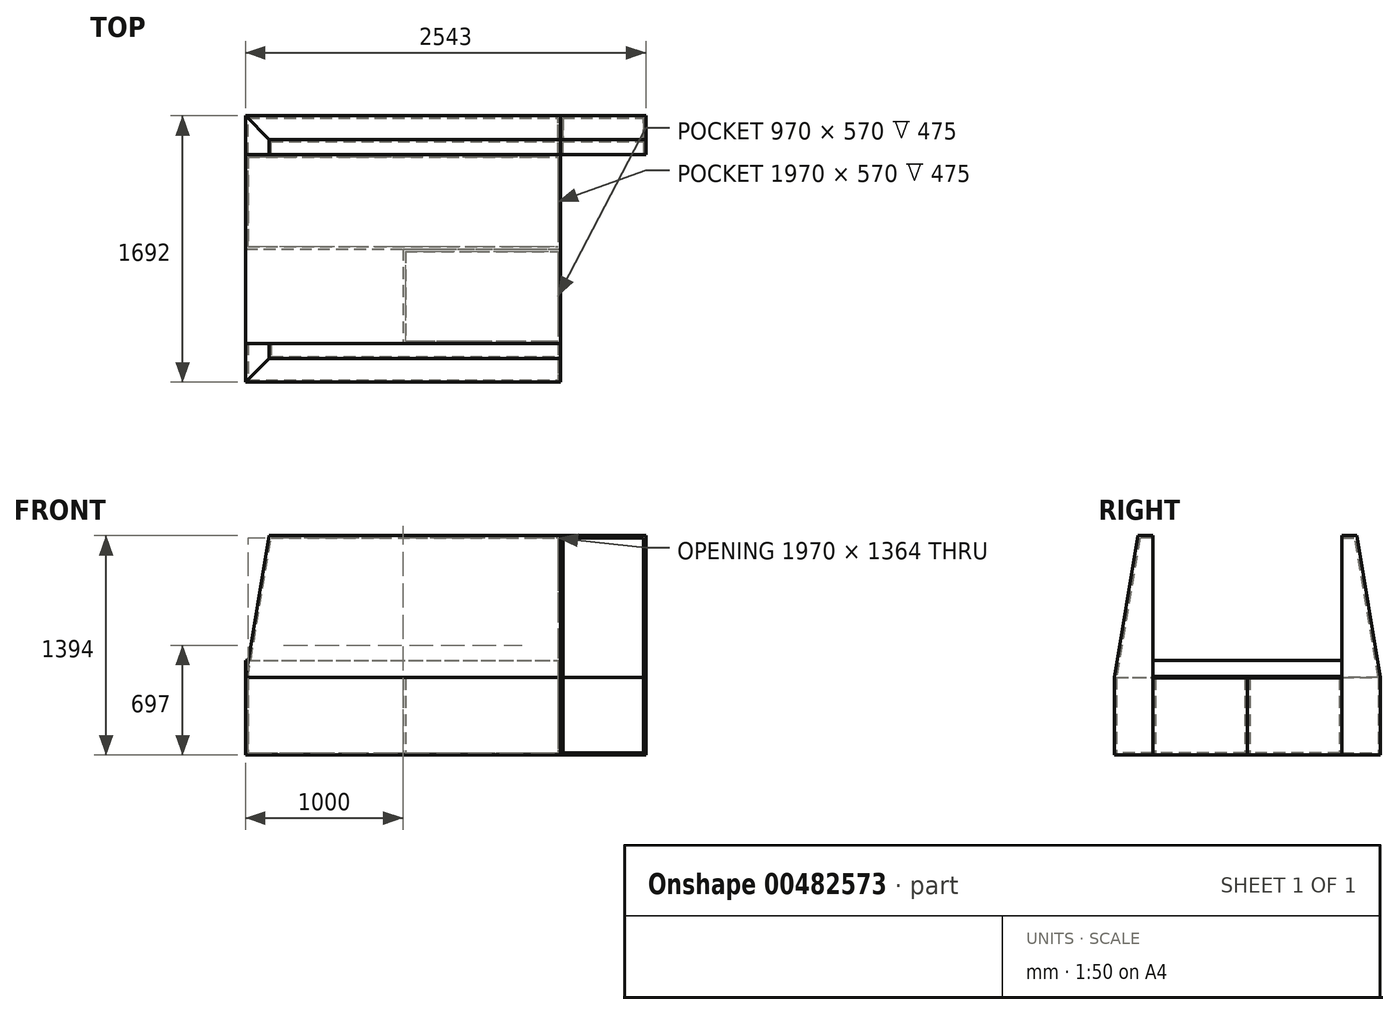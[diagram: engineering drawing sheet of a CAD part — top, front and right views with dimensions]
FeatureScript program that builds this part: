
annotation { "Feature Type Name" : "Feature", "Feature Type Description" : "" }
export const myFeature = defineFeature(function(context is Context, id is Id, definition is map)
    precondition{}
    {
        {
            var Q0;
            Q0=qCreatedBy(makeId("Top.planeOp"),FACE);
            var sketch = newSketch(context, id + "F0", { "sketchPlane" : qUnion([Q0])});
            skLineSegment(sketch, "E0.bottom", {"start": v(1471.5, -846) * mm, "end": v(-1471.5, -846) * mm, "construction": true});
            skLineSegment(sketch, "E0.top", {"start": v(1471.5, 846) * mm, "end": v(-1471.5, 846) * mm, "construction": true});
            skLineSegment(sketch, "E0.left", {"start": v(1471.5, -846) * mm, "end": v(1471.5, 846) * mm, "construction": true});
            skLineSegment(sketch, "E0.right", {"start": v(-1471.5, -846) * mm, "end": v(-1471.5, 846) * mm, "construction": true});
            skLineSegment(sketch, "E1", {"start": v(1071.5, 846) * mm, "end": v(1071.5, -846) * mm, "construction": true});
            skSolve(sketch);
        }
        {
            var Q0;
            Q0=qCreatedBy(makeId("Top.planeOp"),FACE);
            cPlane(context, id + "F1", {"entities" : qUnion([Q0]), "cplaneType" : CPlaneType.OFFSET, "offset" : 1394 * mm, "width" : 150 * mm, "height" : 150 * mm});
        }
        {
            var Q0;
            Q0=qCreatedBy(makeId("Top.planeOp"),FACE);
            var sketch = newSketch(context, id + "F2", { "sketchPlane" : qUnion([Q0])});
            skLineSegment(sketch, "E2.bottom", {"start": v(-1471.5, 600) * mm, "end": v(528.5, 600) * mm});
            skLineSegment(sketch, "E2.top", {"start": v(-1471.5, -600) * mm, "end": v(528.5, -600) * mm});
            skLineSegment(sketch, "E2.left", {"start": v(-1471.5, 600) * mm, "end": v(-1471.5, -600) * mm});
            skLineSegment(sketch, "E2.right", {"start": v(528.5, 600) * mm, "end": v(528.5, -600) * mm});
            skPoint(sketch, "E3", {"position": v(-1471.5, 0) * mm});
            skLineSegment(sketch, "E4.top", {"start": v(-1471.5, 846) * mm, "end": v(528.5, 846) * mm});
            skLineSegment(sketch, "E4.left", {"start": v(-1471.5, 600) * mm, "end": v(-1471.5, 846) * mm});
            skLineSegment(sketch, "E4.right", {"start": v(528.5, 600) * mm, "end": v(528.5, 846) * mm});
            skLineSegment(sketch, "E5.top", {"start": v(-1471.5, -846) * mm, "end": v(528.5, -846) * mm});
            skLineSegment(sketch, "E5.left", {"start": v(-1471.5, -600) * mm, "end": v(-1471.5, -846) * mm});
            skLineSegment(sketch, "E5.right", {"start": v(528.5, -600) * mm, "end": v(528.5, -846) * mm});
            skLineSegment(sketch, "E6", {"start": v(-1471.5, 0) * mm, "end": v(528.5, 0) * mm});
            skLineSegment(sketch, "E7.bottom", {"start": v(528.5, 846) * mm, "end": v(1071.5, 846) * mm});
            skLineSegment(sketch, "E7.top", {"start": v(528.5, 600) * mm, "end": v(1071.5, 600) * mm});
            skLineSegment(sketch, "E7.left", {"start": v(528.5, 846) * mm, "end": v(528.5, 600) * mm});
            skLineSegment(sketch, "E7.right", {"start": v(1071.5, 846) * mm, "end": v(1071.5, 600) * mm});
            skLineSegment(sketch, "E8", {"start": v(-471.5, 0) * mm, "end": v(-471.5, -846) * mm});
            skSolve(sketch);
        }
        {
            var Q0;
            Q0=makeQuery(id+"F2.imprint","IMPRINT",FACE,{"disambiguationData":[TD([[makeQuery(id+"F2.imprint","IMPRINT",EDGE,{"derivedFrom":sQuery(id+"F2.wireOp",EDGE,"E2.left")}),1.0]])]});
            var Q1;
            {var subQ1=sQuery(id+"F2.wireOp",EDGE,"E2.right");var subQ3=sQuery(id+"F2.wireOp",EDGE,"E6");var subQ4=makeQuery(id+"F2.imprint","INTERSECT",VERTEX,{"derivedFrom":[subQ1,subQ3]});Q1=makeQuery(id+"F2.imprint","IMPRINT",FACE,{"disambiguationData":[TD([[makeQuery(id+"F2.imprint","IMPRINT",EDGE,{"disambiguationData":[TD([[subQ4,1.0]])],"derivedFrom":subQ3}),-1.0]])]});}
            var Q2;
            {var subQ4=sQuery(id+"F2.wireOp",EDGE,"E2.bottom");Q2=makeQuery(id+"F2.imprint","IMPRINT",FACE,{"disambiguationData":[TD([[makeQuery(id+"F2.imprint","IMPRINT",EDGE,{"derivedFrom":subQ4}),-1.0]])]});}
            extrude(context, id + "F3", {"entities" : qUnion([Q0, Q1, Q2]), "depth" : 600 * mm});
        }
        {
            var Q0;
            Q0=makeQuery(id+"F2.imprint","IMPRINT",FACE,{"disambiguationData":[TD([[makeQuery(id+"F2.imprint","IMPRINT",EDGE,{"derivedFrom":sQuery(id+"F2.wireOp",EDGE,"E2.bottom")}),1.0]])]});
            var Q1;
            Q1=makeQuery(id+"F2.imprint","IMPRINT",FACE,{"disambiguationData":[TD([[makeQuery(id+"F2.imprint","IMPRINT",EDGE,{"derivedFrom":sQuery(id+"F2.wireOp",EDGE,"E2.top")}),-1.0]])]});
            extrude(context, id + "F4", {"entities" : qUnion([Q0, Q1]), "depth" : 1394 * mm});
        }
        {
            var Q0;
            {var subQ1=sQuery(id+"F2.wireOp",EDGE,"E2.left");var subQ3=sQuery(id+"F2.wireOp",EDGE,"E6");var subQ4=makeQuery(id+"F2.imprint","INTERSECT",VERTEX,{"derivedFrom":[subQ1,subQ3]});Q0=makeQuery(id+"F2.imprint","IMPRINT",FACE,{"disambiguationData":[TD([[makeQuery(id+"F2.imprint","IMPRINT",EDGE,{"disambiguationData":[TD([[subQ4,-1.0]])],"derivedFrom":subQ3}),-1.0]])]});}
            var Q1;
            {var subQ1=sQuery(id+"F2.wireOp",EDGE,"E2.right");var subQ3=sQuery(id+"F2.wireOp",EDGE,"E6");var subQ4=makeQuery(id+"F2.imprint","INTERSECT",VERTEX,{"derivedFrom":[subQ1,subQ3]});Q1=makeQuery(id+"F2.imprint","IMPRINT",FACE,{"disambiguationData":[TD([[makeQuery(id+"F2.imprint","IMPRINT",EDGE,{"disambiguationData":[TD([[subQ4,1.0]])],"derivedFrom":subQ3}),-1.0]])]});}
            var Q2;
            {var subQ4=sQuery(id+"F2.wireOp",EDGE,"E2.bottom");Q2=makeQuery(id+"F2.imprint","IMPRINT",FACE,{"disambiguationData":[TD([[makeQuery(id+"F2.imprint","IMPRINT",EDGE,{"derivedFrom":subQ4}),-1.0]])]});}
            extrude(context, id + "F5", {"entities" : qUnion([Q0, Q1, Q2]), "operationType" : NewBodyOperationType.REMOVE, "depth" : 500 * mm});
        }
        {
            var Q0;
            Q0=makeQuery(id+"F2.imprint","IMPRINT",FACE,{"disambiguationData":[TD([[makeQuery(id+"F2.imprint","IMPRINT",EDGE,{"derivedFrom":sQuery(id+"F2.wireOp",EDGE,"E7.bottom")}),-1.0]])]});
            extrude(context, id + "F6", {"entities" : qUnion([Q0]), "depth" : 1394 * mm});
        }
        {
            var Q0;
            Q0=makeQuery(id+"F4.opExtrude","CAP_EDGE",EDGE,{"disambiguationData":[OSD([sQuery(id+"F2.wireOp",EDGE,"E5.top")])],"isStart":false});
            var Q1;
            Q1=makeQuery(id+"F4.opExtrude","CAP_EDGE",EDGE,{"disambiguationData":[OSD([sQuery(id+"F2.wireOp",EDGE,"E5.left")])],"isStart":false});
            chamfer(context, id + "F7", {"entities" : qUnion([Q0, Q1]), "chamferType" : ChamferType.TWO_OFFSETS, "width1" : 150 * mm, "oppositeDirection" : false, "width2" : 900 * mm, "tangentPropagation" : true});
        }
        {
            var Q0;
            Q0=makeQuery(id+"F4.opExtrude","CAP_EDGE",EDGE,{"disambiguationData":[OSD([sQuery(id+"F2.wireOp",EDGE,"E4.top")])],"isStart":false});
            var Q1;
            Q1=makeQuery(id+"F6.opExtrude","CAP_EDGE",EDGE,{"disambiguationData":[OSD([sQuery(id+"F2.wireOp",EDGE,"E7.bottom")])],"isStart":false});
            var Q2;
            Q2=makeQuery(id+"F4.opExtrude","CAP_EDGE",EDGE,{"disambiguationData":[OSD([sQuery(id+"F2.wireOp",EDGE,"E4.left")])],"isStart":false});
            chamfer(context, id + "F8", {"entities" : qUnion([Q0, Q1, Q2]), "chamferType" : ChamferType.TWO_OFFSETS, "width1" : 900 * mm, "oppositeDirection" : false, "width2" : 150 * mm, "tangentPropagation" : true});
        }
        {
            var Q0;
            {var subQ1=sQuery(id+"F2.wireOp",EDGE,"E2.right");var subQ3=sQuery(id+"F2.wireOp",EDGE,"E6");var subQ4=makeQuery(id+"F2.imprint","INTERSECT",VERTEX,{"derivedFrom":[subQ1,subQ3]});Q0=makeQuery(id+"F2.imprint","IMPRINT",FACE,{"disambiguationData":[TD([[makeQuery(id+"F2.imprint","IMPRINT",EDGE,{"disambiguationData":[TD([[subQ4,1.0]])],"derivedFrom":subQ3}),-1.0]])]});}
            extrude(context, id + "F9", {"entities" : qUnion([Q0]), "depth" : 490 * mm});
        }
        {
            var Q0;
            {var subQ0=sQuery(id+"F2.wireOp",EDGE,"E2.bottom");Q0=makeQuery(id+"F2.imprint","IMPRINT",FACE,{"disambiguationData":[TD([[makeQuery(id+"F2.imprint","IMPRINT",EDGE,{"derivedFrom":subQ0}),-1.0]])]});}
            extrude(context, id + "F10", {"entities" : qUnion([Q0]), "depth" : 490 * mm});
        }
        {
            var Q0;
            Q0=makeQuery(id+"F10.opExtrude","CAP_FACE",FACE,{"disambiguationData":[OSD([sQuery(id+"F2.wireOp",EDGE,"E2.left"),sQuery(id+"F2.wireOp",EDGE,"E2.right"),sQuery(id+"F2.wireOp",EDGE,"E4.top"),sQuery(id+"F2.wireOp",EDGE,"E4.left"),sQuery(id+"F2.wireOp",EDGE,"E6"),sQuery(id+"F2.wireOp",EDGE,"E7.left")])],"isStart":false});
            var Q1;
            Q1=makeQuery(id+"F9.opExtrude","CAP_FACE",FACE,{"disambiguationData":[OSD([sQuery(id+"F2.wireOp",EDGE,"E2.left"),sQuery(id+"F2.wireOp",EDGE,"E2.right"),sQuery(id+"F2.wireOp",EDGE,"E5.top"),sQuery(id+"F2.wireOp",EDGE,"E5.left"),sQuery(id+"F2.wireOp",EDGE,"E5.right"),sQuery(id+"F2.wireOp",EDGE,"E6")])],"isStart":false});
            var Q2;
            Q2=makeQuery(id+"F4.opExtrude","SWEPT_FACE",FACE,{"disambiguationData":[OSD([sQuery(id+"F2.wireOp",EDGE,"E2.top")])]});
            var Q3;
            Q3=makeQuery(id+"F4.opExtrude","SWEPT_FACE",FACE,{"disambiguationData":[OSD([sQuery(id+"F2.wireOp",EDGE,"E2.bottom")])]});
            var Q4;
            Q4=makeQuery(id+"F6.opExtrude","SWEPT_FACE",FACE,{"disambiguationData":[OSD([sQuery(id+"F2.wireOp",EDGE,"E7.top")])]});
            shell(context, id + "F11", {"entities" : qUnion([Q0, Q1, Q2, Q3, Q4]), "thickness" : 15 * mm});
        }
    });
